# Revit family: BAS-IP_Модуль подключения Wiegand_SH-12
name_source: partatom
category: Устройства связи
units: mm (PartAtom-declared; Revit-internal decimal feet)

## family parameters
Всегда вертикально = Да
На основе рабочей плоскости = Нет
Общий = Нет
При загрузке вырезать с полостями = Нет
Размер круглого соединителя = Использовать диаметр
Сохранять ориентацию аннотаций = Нет
Тип детали = Нормальный
Точка расчета площади = Нет

## types (1)
- SH-12
    ADSK_Единица измерения = шт.
    ADSK_Завод-изготовитель = BAS-IP
    ADSK_Количество = 1
    ADSK_Марка = SH-12
    ADSK_Материал = White
    ADSK_Наименование = Модуль подключения внешних устройств к панелям BAS-IP по интерфейсу Wiegand
    Габаритные размеры = 82 × 56 × 34 мм
    Габаритные размеры с креплениями = 115 × 56 × 34 мм
    Допустимая влажность = 20 – 80 %
    Изготовитель = BAS-IP
    Интерфейс подключения контроллеров = Wiegand 26, 34, 58, 64, 66 бит
    Интерфейс подключения считывателей = Wiegand 26, 34, 58, 64, 66 бит
    Интерфейс подключния к панелям BAS-IP = RS485 (A&B)
    Класс степени защиты = IP30C
    Масса = 0,11 кг
    Напряжение питания = +12 В
    Температура хранения = -15 – +65 °С
    Температура эксплуатации = -40 – +70 °С
    Ток потребления = 0,15 А
